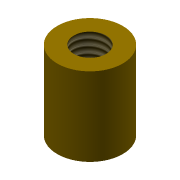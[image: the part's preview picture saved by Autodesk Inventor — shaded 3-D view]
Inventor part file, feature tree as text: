
AUTODESK INVENTOR PART (.ipt)
format: ipt  version: 2022 (Build 260153000, 153)  size: 81,920 bytes
history: native  units: mm
features: sketch x2, extrude x1, hole x1
ambient origin geometry x8: Origin, YZ Plane, XZ Plane, XY Plane, X Axis, Y Axis, Z Axis, Center Point
bodies: Solid1 (feature_tree)
feature tree (4):
  extrude  "Extrusion1"  Depth=6.0mm TaperAngle=0.0deg
  hole  "Hole1"  [1 undecoded]
  sketch  "Sketch1"  dims[d0=5.0mm d1=6.0mm d2=0.0mm]
  sketch  "Sketch2"  dims[d3=2.459mm d4=10.0mm d5=4.0mm d6=2.0mm d7=90.0deg d8=8.0mm d9=20.594885mm]
note: 1 required parameter value undecoded (feature->parameter linkage not recoverable at this tier; creation-order binding heuristic only, values carry confidence <= 0.55)
